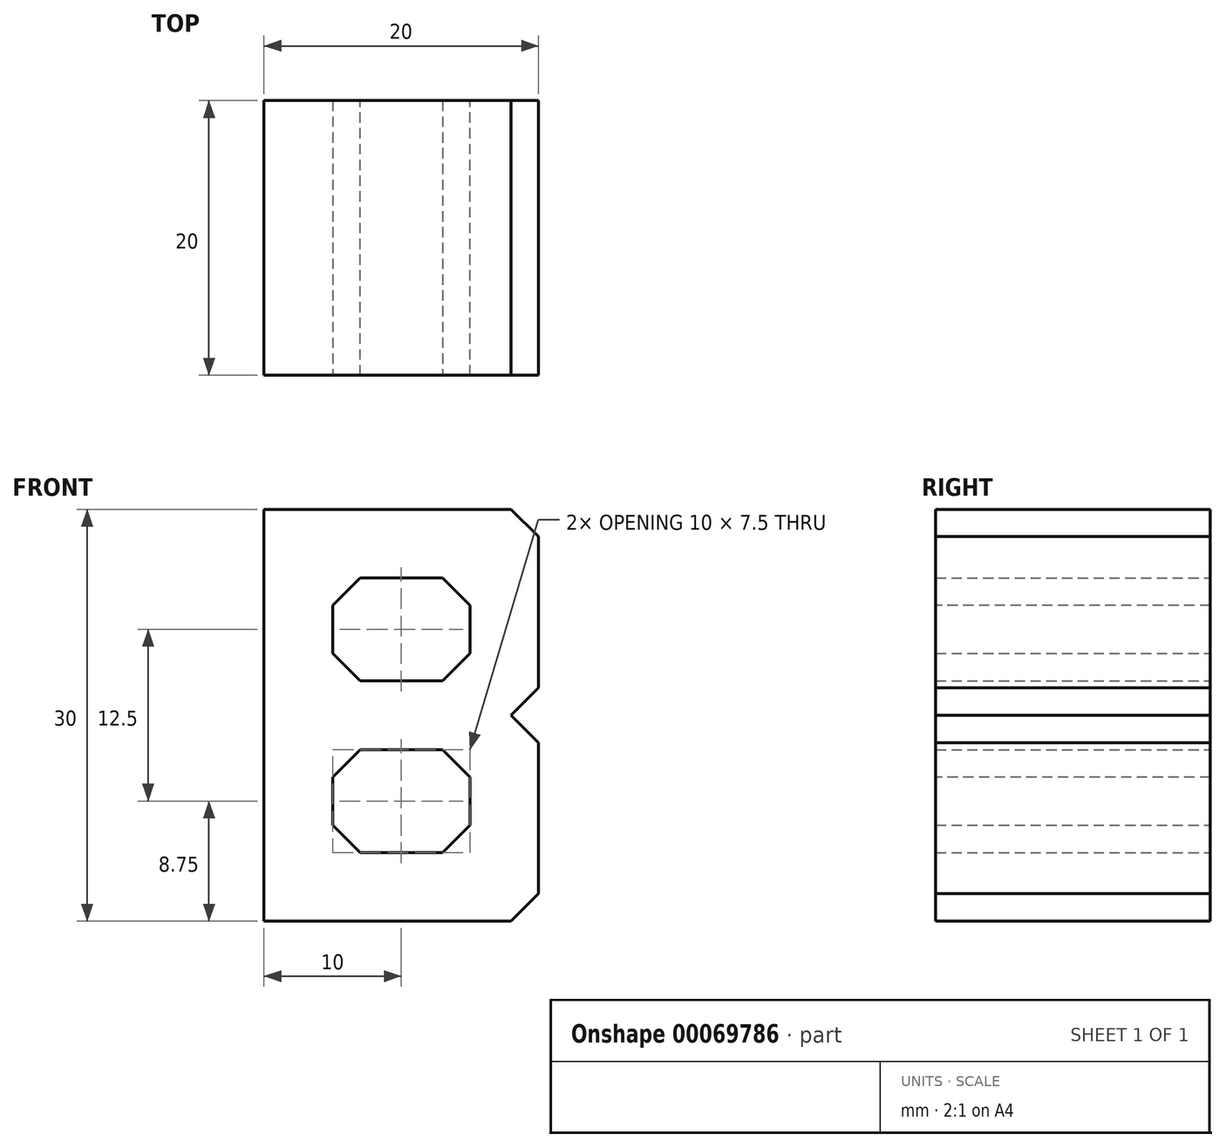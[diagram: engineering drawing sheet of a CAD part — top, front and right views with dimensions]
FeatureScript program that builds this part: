
annotation { "Feature Type Name" : "Feature", "Feature Type Description" : "" }
export const myFeature = defineFeature(function(context is Context, id is Id, definition is map)
    precondition{}
    {
        {
            var Q0;
            Q0=qCreatedBy(makeId("Front.planeOp"),FACE);
            var sketch = newSketch(context, id + "F0", { "sketchPlane" : qUnion([Q0])});
            skLineSegment(sketch, "E0.top", {"start": v(0, 30) * mm, "end": v(20, 30) * mm});
            skLineSegment(sketch, "E0.left", {"start": v(0, 0) * mm, "end": v(0, 30) * mm});
            skLineSegment(sketch, "E1", {"start": v(5, 25) * mm, "end": v(5, 17.5) * mm});
            skLineSegment(sketch, "E2", {"start": v(15, 25) * mm, "end": v(15, 17.5) * mm});
            skLineSegment(sketch, "E3", {"start": v(5, 25) * mm, "end": v(15, 25) * mm});
            skLineSegment(sketch, "E4", {"start": v(5, 17.5) * mm, "end": v(15, 17.5) * mm});
            skPoint(sketch, "E5.start.orphan", {"position": v(0, 15) * mm});
            skLineSegment(sketch, "E6.trimOffspring", {"start": v(5, 12.5) * mm, "end": v(5, 5) * mm});
            skLineSegment(sketch, "E7", {"start": v(5, 12.5) * mm, "end": v(15, 12.5) * mm});
            skLineSegment(sketch, "E8", {"start": v(15, 5) * mm, "end": v(15, 12.5) * mm});
            skLineSegment(sketch, "E9", {"start": v(5, 5) * mm, "end": v(15, 5) * mm});
            skLineSegment(sketch, "E10", {"start": v(20, 30) * mm, "end": v(20, 15) * mm});
            skLineSegment(sketch, "E11", {"start": v(20, 15) * mm, "end": v(20, 0) * mm});
            skLineSegment(sketch, "E12", {"start": v(0, 0) * mm, "end": v(20, 0) * mm});
            skSolve(sketch);
        }
        {
            var Q0;
            Q0=makeQuery(id+"F0.imprint","IMPRINT",FACE,{"disambiguationData":[TD([[makeQuery(id+"F0.imprint","IMPRINT",EDGE,{"derivedFrom":sQuery(id+"F0.wireOp",EDGE,"E0.bottom")}),1.0]])]});
            var Q1;
            Q1=makeQuery(id+"F0.imprint","IMPRINT",FACE,{"disambiguationData":[TD([[makeQuery(id+"F0.imprint","IMPRINT",EDGE,{"derivedFrom":sQuery(id+"F0.wireOp",EDGE,"E0.top")}),-1.0]])]});
            extrude(context, id + "F1", {"entities" : qUnion([Q0, Q1]), "depth" : 20 * mm});
        }
        {
            var Q0;
            Q0=makeQuery(id+"F1.opExtrude","SWEPT_EDGE",EDGE,{"disambiguationData":[OSD([sQuery(id+"F0.wireOp",EDGE,"E0.top"),sQuery(id+"F0.wireOp",EDGE,"E10")])]});
            var Q1;
            Q1=makeQuery(id+"F1.opExtrude","SWEPT_EDGE",EDGE,{"disambiguationData":[OSD([sQuery(id+"F0.wireOp",EDGE,"E1"),sQuery(id+"F0.wireOp",EDGE,"E4")])]});
            var Q2;
            Q2=makeQuery(id+"F1.opExtrude","SWEPT_EDGE",EDGE,{"disambiguationData":[OSD([sQuery(id+"F0.wireOp",EDGE,"E1"),sQuery(id+"F0.wireOp",EDGE,"E3")])]});
            var Q3;
            Q3=makeQuery(id+"F1.opExtrude","SWEPT_EDGE",EDGE,{"disambiguationData":[OSD([sQuery(id+"F0.wireOp",EDGE,"E6.trimOffspring"),sQuery(id+"F0.wireOp",EDGE,"E7")])]});
            var Q4;
            Q4=makeQuery(id+"F1.opExtrude","SWEPT_EDGE",EDGE,{"disambiguationData":[OSD([sQuery(id+"F0.wireOp",EDGE,"E6.trimOffspring"),sQuery(id+"F0.wireOp",EDGE,"E9")])]});
            var Q5;
            Q5=makeQuery(id+"F1.opExtrude","SWEPT_EDGE",EDGE,{"disambiguationData":[OSD([sQuery(id+"F0.wireOp",EDGE,"E2"),sQuery(id+"F0.wireOp",EDGE,"E3")])]});
            var Q6;
            Q6=makeQuery(id+"F1.opExtrude","SWEPT_EDGE",EDGE,{"disambiguationData":[OSD([sQuery(id+"F0.wireOp",EDGE,"E2"),sQuery(id+"F0.wireOp",EDGE,"E4")])]});
            var Q7;
            Q7=makeQuery(id+"F1.opExtrude","SWEPT_EDGE",EDGE,{"disambiguationData":[OSD([sQuery(id+"F0.wireOp",EDGE,"E7"),sQuery(id+"F0.wireOp",EDGE,"E8")])]});
            var Q8;
            Q8=makeQuery(id+"F1.opExtrude","SWEPT_EDGE",EDGE,{"disambiguationData":[OSD([sQuery(id+"F0.wireOp",EDGE,"E8"),sQuery(id+"F0.wireOp",EDGE,"E9")])]});
            var Q9;
            Q9=makeQuery(id+"F1.opExtrude","SWEPT_EDGE",EDGE,{"disambiguationData":[OSD([sQuery(id+"F0.wireOp",EDGE,"E11"),sQuery(id+"F0.wireOp",EDGE,"E12")])]});
            chamfer(context, id + "F2", {"entities" : qUnion([Q0, Q1, Q2, Q3, Q4, Q5, Q6, Q7, Q8, Q9]), "width" : 2 * mm, "tangentPropagation" : true});
        }
        {
            var Q0;
            Q0=makeQuery(id+"F1.opExtrude","CAP_FACE",FACE,{"disambiguationData":[OSD([sQuery(id+"F0.wireOp",EDGE,"E0.top"),sQuery(id+"F0.wireOp",EDGE,"E0.left"),sQuery(id+"F0.wireOp",EDGE,"E1"),sQuery(id+"F0.wireOp",EDGE,"E2"),sQuery(id+"F0.wireOp",EDGE,"E3"),sQuery(id+"F0.wireOp",EDGE,"E4"),sQuery(id+"F0.wireOp",EDGE,"E6.trimOffspring"),sQuery(id+"F0.wireOp",EDGE,"E7"),sQuery(id+"F0.wireOp",EDGE,"E8"),sQuery(id+"F0.wireOp",EDGE,"E9"),sQuery(id+"F0.wireOp",EDGE,"E10"),sQuery(id+"F0.wireOp",EDGE,"E11"),sQuery(id+"F0.wireOp",EDGE,"E12")])],"isStart":false});
            var sketch = newSketch(context, id + "F3", { "sketchPlane" : qUnion([Q0])});
            skLineSegment(sketch, "E13", {"start": v(20, 15) * mm, "end": v(18, 15) * mm});
            skPoint(sketch, "E13.endSnap0", {"position": v(20, 15) * mm});
            skLineSegment(sketch, "E14", {"start": v(18, 15) * mm, "end": v(20, 17) * mm});
            skLineSegment(sketch, "E15", {"start": v(20, 17) * mm, "end": v(20, 13) * mm});
            skLineSegment(sketch, "E16", {"start": v(20, 13) * mm, "end": v(18, 15) * mm});
            skSolve(sketch);
        }
        {
            var Q0;
            {var subQ0=sQuery(id+"F3.wireOp",EDGE,"E13");Q0=makeQuery(id+"F3.imprint","IMPRINT",FACE,{"disambiguationData":[TD([[makeQuery(id+"F3.imprint","IMPRINT",EDGE,{"derivedFrom":subQ0}),1.0]])]});}
            var Q1;
            {var subQ0=sQuery(id+"F3.wireOp",EDGE,"E13");Q1=makeQuery(id+"F3.imprint","IMPRINT",FACE,{"disambiguationData":[TD([[makeQuery(id+"F3.imprint","IMPRINT",EDGE,{"derivedFrom":subQ0}),-1.0]])]});}
            extrude(context, id + "F4", {"entities" : qUnion([Q0, Q1]), "operationType" : NewBodyOperationType.REMOVE, "oppositeDirection" : true, "depth" : 25 * mm});
        }
    });
